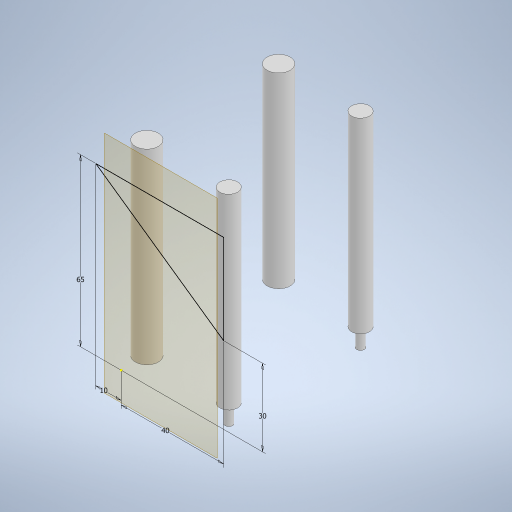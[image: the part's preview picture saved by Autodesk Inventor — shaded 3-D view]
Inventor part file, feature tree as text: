
AUTODESK INVENTOR PART (.ipt)
format: ipt  version: 2024 (Build 280153000, 153)  size: 284,672 bytes
history: native  units: mm
features: sketch x7, extrude x4, plane x1
ambient origin geometry x8: Origin, YZ Plane, XZ Plane, XY Plane, X Axis, Y Axis, Z Axis, Center Point
bodies: Solid1 (feature_tree)
feature tree (12):
  extrude  "Extrusion1"  Depth=6.5mm
  extrude  "Extrusion2"  Depth=9.0mm
  sketch  "Sketch3"  dims[d4=7.0mm d5=7.0mm]
  extrude  "Extrusion3"  Depth=7.0mm
  extrude  "Extrusion4"  Depth=32.0mm
  plane  "Work Plane1"
  sketch  "Sketch7"  dims[d10=3.0mm]
  sketch  "Sketch8"  dims[d11=3.0mm d12=7.0mm d13=0.0mm d14=7.0mm d15=0.0mm d16=60.0mm d17=0.0mm d18=7.0mm d19=7.0mm d20=9.0mm d21=9.0mm d22=10.0mm d23=30.0mm d24=65.0mm d25=10.0mm d26=40.0mm]
  sketch  "Sketch1"  dims[d0=9.0mm d1=6.5mm]
  sketch  "Sketch2"  dims[d2=6.5mm d3=9.0mm]
  sketch  "Sketch4"  dims[d6=51.5mm d7=32.0mm]
  sketch  "Sketch5"  dims[d8=6.0mm d9=0.0mm]
